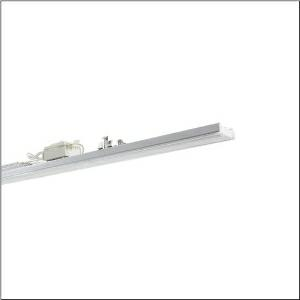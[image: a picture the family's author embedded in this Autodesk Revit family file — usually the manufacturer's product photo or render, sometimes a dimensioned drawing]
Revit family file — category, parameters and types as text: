
# Revit family: licross_r__21_recessed_mo_52tl12dn68xg_864e
name_source: partatom
category: Lighting Fixtures
units: mm (PartAtom-declared; Revit-internal decimal feet)

## family parameters
Cut with Voids When Loaded = No
Host = Face
Light Source = No
Part Type = Normal
Room Calculation Point = No
Round Connector Dimension = Use Diameter
Shared = No

## types (1)
- --- (1 x LED, 8000 lm, 45.6 W, 6500K)
    Apparent Load = 46 VA
    CIE Flux Codes = 72 92 99 100 100
    Color Rendering = 80
    Color Temperature = 6500K
    Default Elevation = 1800 mm
    Description = Licross® 21 Recessed MO, luminaire insert, of sheet steel, galvanised, coil coated, white, length: 1.500mm, width: 66mm, height: 67mm, LED rated luminous flux: 8.000lm, light colour: 865, control gear: DALI 2, with plug, 5-pole, with phase selection, mains connection: 220..240V, AC, 50/60Hz, rated input power: 46W, internal wiring halogen-free, primary optical cover: cover, of PMMA, light emission: direct distribution, primary light characteristic: symmetric, protection rating (complete): IP40, insulation class (complete): insulation class I (protective earthing), certification: CE, ENEC, VDE, UKCA, protection symbol: D if used in an environment without relevant dust loads with corresponding accessories, impact resistance: IK06, permissible ambient temperature for indoor applications: -25..+40°C, corresponds to IFS (International Featured Standards) requirements for safety and quality in the food industry, reducing of maximum allowable ambient temperature of 5°C with ceiling mounting, LABS conformity tested according to VDMA 24364:2018-05, packaging unit: 1 piece
    Height = 58 mm
    Lamp = 1 x LED
    Lamp Light Flux = 8000 lm
    Lamp Power = 45.6 W
    Lamp count = 1
    Length = 1500 mm
    Luminous efficacy = 175 lm/W
    Manufacturer = Siteco
    ModVariant = No
    Model = 52TL12DN68XG
    Mounting Place = Ceiling
    Mounting Type = Pendant
    Number of Poles = 1
    OnlyDefault = Yes
    Power Factor = 1
    Product Name = Licross® 21 Recessed MO
    Product group = luminaire insert | ceiling pendant
    ProductGroupID = 902
    Protection Class = Protection class I
    Protection Degree = IP 40
    RLX_Detail_Level = 1
    RLX_Emergency_Light_Flux = 0 lm
    RLX_Emergency_Type = 0
    RLX_Emergency_Type_DB = No
    RlxData = <blob elided: 24553 chars, md5=70ef12e5>
    Socket = socket
    Standby Power = 0 W
    System Light Flux = 8000 lm
    System Power = 46 W
    Type Comments = factory setting: luminous flux: 100 % | dim-lin: 254 | 306 mA
    Type Image = l_1296930.jpg
    URL = http://relux.com
    VarID = @adj_030323
    Voltage = 0 V
    Weight = 0.00 kg
    Width = 66 mm

## geometry (parser evidence)
native form markers: Blend x4, Sweep x9
no freeform markers — native parametric forms only
